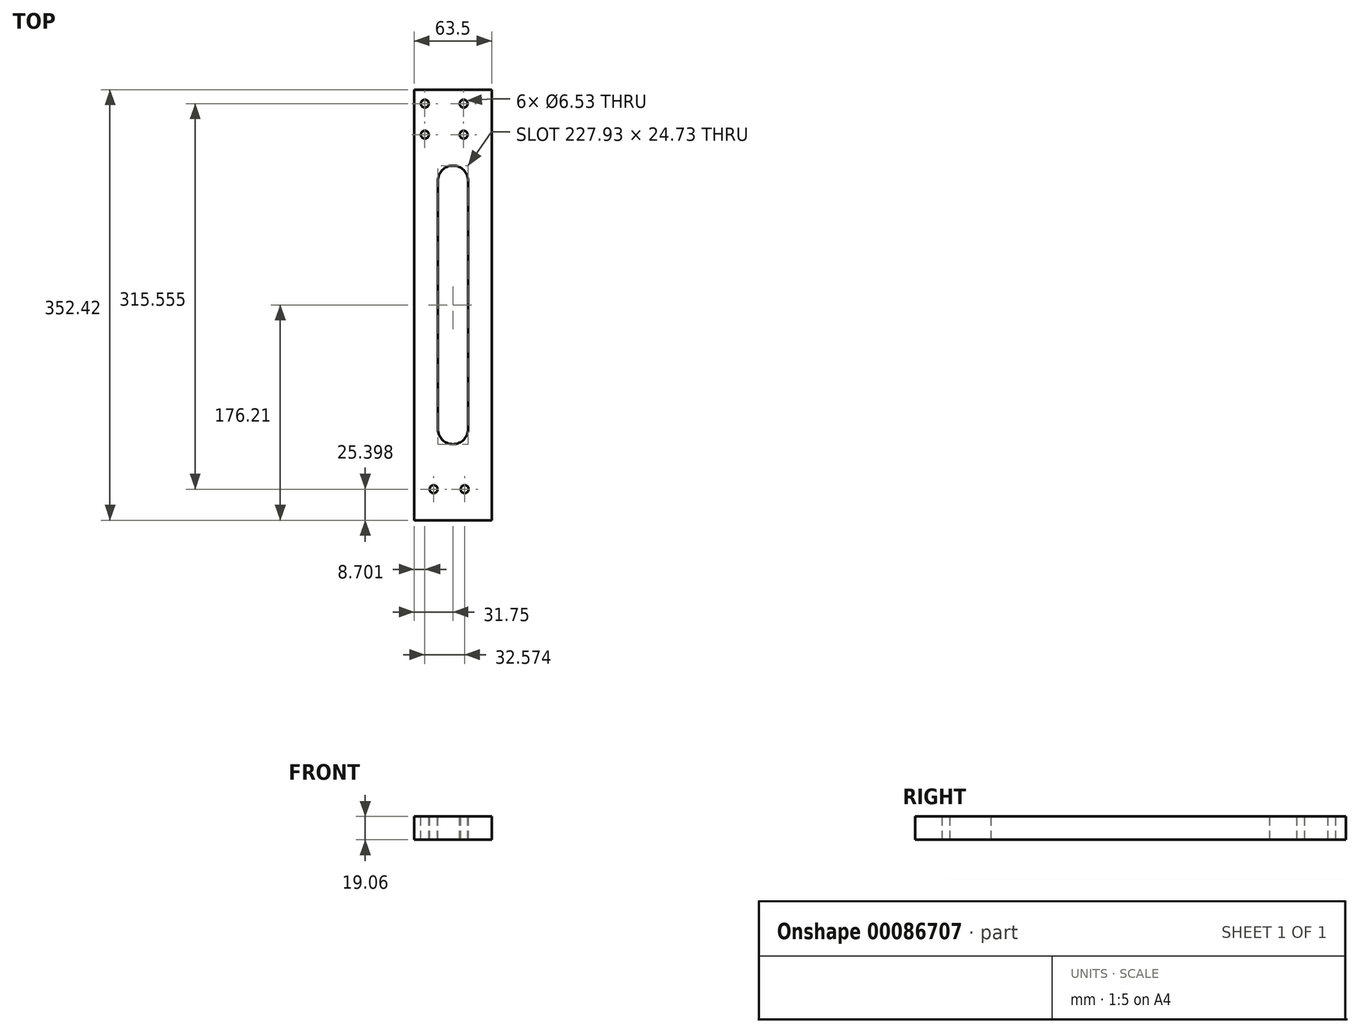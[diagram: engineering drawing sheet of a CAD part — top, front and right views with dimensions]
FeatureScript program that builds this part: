
annotation { "Feature Type Name" : "Feature", "Feature Type Description" : "" }
export const myFeature = defineFeature(function(context is Context, id is Id, definition is map)
    precondition{}
    {
        {
            var Q0;
            Q0=qCreatedBy(makeId("Front.planeOp"),FACE);
            var sketch = newSketch(context, id + "F0", { "sketchPlane" : qUnion([Q0])});
            skLineSegment(sketch, "E0.bottom", {"start": v(31.75, 9.53) * mm, "end": v(-31.75, 9.53) * mm});
            skLineSegment(sketch, "E0.top", {"start": v(31.75, -9.52) * mm, "end": v(-31.75, -9.52) * mm});
            skLineSegment(sketch, "E0.left", {"start": v(31.75, 9.53) * mm, "end": v(31.75, -9.52) * mm});
            skLineSegment(sketch, "E0.right", {"start": v(-31.75, 9.53) * mm, "end": v(-31.75, -9.52) * mm});
            skPoint(sketch, "E0.middle", {"position": v(0, 0) * mm});
            skSolve(sketch);
        }
        {
            var Q0;
            Q0 = qSketchRegion(id + "F0", true);
            extrude(context, id + "F1", {"entities" : qUnion([Q0]), "endBound" : BoundingType.SYMMETRIC, "depth" : 352.42 * mm});
        }
        {
            var Q0;
            Q0=makeQuery(id+"F1.opExtrude","SWEPT_FACE",FACE,{"disambiguationData":[OSD([sQuery(id+"F0.wireOp",EDGE,"E0.bottom")])]});
            var sketch = newSketch(context, id + "F2", { "sketchPlane" : qUnion([Q0])});
            skPoint(sketch, "E1", {"position": v(-23.05, 164.74) * mm});
            skPoint(sketch, "E2", {"position": v(-23.05, 139.34) * mm});
            skPoint(sketch, "E3", {"position": v(8.7, 139.34) * mm});
            skPoint(sketch, "E4", {"position": v(8.7, 164.74) * mm});
            skPoint(sketch, "E5", {"position": v(9.53, -150.81) * mm});
            skPoint(sketch, "E6", {"position": v(-15.88, -150.81) * mm});
            skLineSegment(sketch, "E7", {"start": v(-31.75, -150.81) * mm, "end": v(31.75, -150.81) * mm, "construction": true});
            skLineSegment(sketch, "E8.bottom", {"start": v(-23.05, 164.74) * mm, "end": v(8.7, 164.74) * mm, "construction": true});
            skLineSegment(sketch, "E8.top", {"start": v(-23.05, 139.34) * mm, "end": v(8.7, 139.34) * mm, "construction": true});
            skLineSegment(sketch, "E8.left", {"start": v(-23.05, 164.74) * mm, "end": v(-23.05, 139.34) * mm, "construction": true});
            skLineSegment(sketch, "E8.right", {"start": v(8.7, 164.74) * mm, "end": v(8.7, 139.34) * mm, "construction": true});
            skSolve(sketch);
        }
        {
            var Q0;
            Q0=sQuery(id+"F2.wireOp",VERTEX,"E4");
            var Q1;
            Q1=sQuery(id+"F2.wireOp",VERTEX,"E3");
            var Q2;
            Q2=sQuery(id+"F2.wireOp",VERTEX,"E2");
            var Q3;
            Q3=sQuery(id+"F2.wireOp",VERTEX,"E1");
            var Q4;
            Q4=sQuery(id+"F2.wireOp",VERTEX,"E6");
            var Q5;
            Q5=sQuery(id+"F2.wireOp",VERTEX,"E5");
            var Q6;
            Q6=makeQuery(id+"F1.opExtrude","SWEPT_BODY",BODY,{"disambiguationData":[OSD([sQuery(id+"F0.wireOp",EDGE,"E0.bottom"),sQuery(id+"F0.wireOp",EDGE,"E0.top"),sQuery(id+"F0.wireOp",EDGE,"E0.left"),sQuery(id+"F0.wireOp",EDGE,"E0.right")])]});
            hole(context, id + "F3", {"style" : HoleStyle.SIMPLE, "endStyle" : HoleEndStyle.THROUGH, "standardTappedOrClearance" : lookupTablePath({ "standard" : "ANSI", "engagement" : "75%", "pitch" : "18 tpi", "size" : "5/16", "type" : "Tapped" }), "standardBlindInLast" : lookupTablePath({ "standard" : "ANSI", "engagement" : "75%", "pitch" : "18 tpi", "size" : "5/16", "type" : "Tapped" }), "holeDiameter" : 6.53 * mm, "locations" : qUnion([Q0, Q1, Q2, Q3, Q4, Q5]), "scope" : qUnion([Q6]), "isTappedThrough" : true, "majorDiameter" : 7.94 * mm, "showTappedDepth" : true});
        }
        {
            var Q0;
            Q0=makeQuery(id+"F1.opExtrude","SWEPT_FACE",FACE,{"disambiguationData":[OSD([sQuery(id+"F0.wireOp",EDGE,"E0.bottom")])]});
            var sketch = newSketch(context, id + "F4", { "sketchPlane" : qUnion([Q0])});
            skLineSegment(sketch, "E9", {"start": v(-12.37, -101.6) * mm, "end": v(-12.37, 101.6) * mm});
            skLineSegment(sketch, "E10", {"start": v(12.37, 101.6) * mm, "end": v(12.37, -101.6) * mm});
            skArc(sketch, "E11", {"start": v(-12.37, -101.6) * mm, "mid": v(0, -113.97) * mm, "end": v(12.37, -101.6) * mm});
            skArc(sketch, "E12", {"start": v(12.37, 101.6) * mm, "mid": v(0, 113.97) * mm, "end": v(-12.37, 101.6) * mm});
            skSolve(sketch);
        }
        {
            var Q0;
            Q0=makeQuery(id+"F4.imprint","IMPRINT",FACE,{"disambiguationData":[TD([[makeQuery(id+"F4.imprint","IMPRINT",EDGE,{"derivedFrom":sQuery(id+"F4.wireOp",EDGE,"E9")}),-1.0]])]});
            extrude(context, id + "F5", {"entities" : qUnion([Q0]), "operationType" : NewBodyOperationType.REMOVE, "endBound" : BoundingType.THROUGH_ALL, "oppositeDirection" : true, "depth" : 25.4 * mm});
        }
    });
